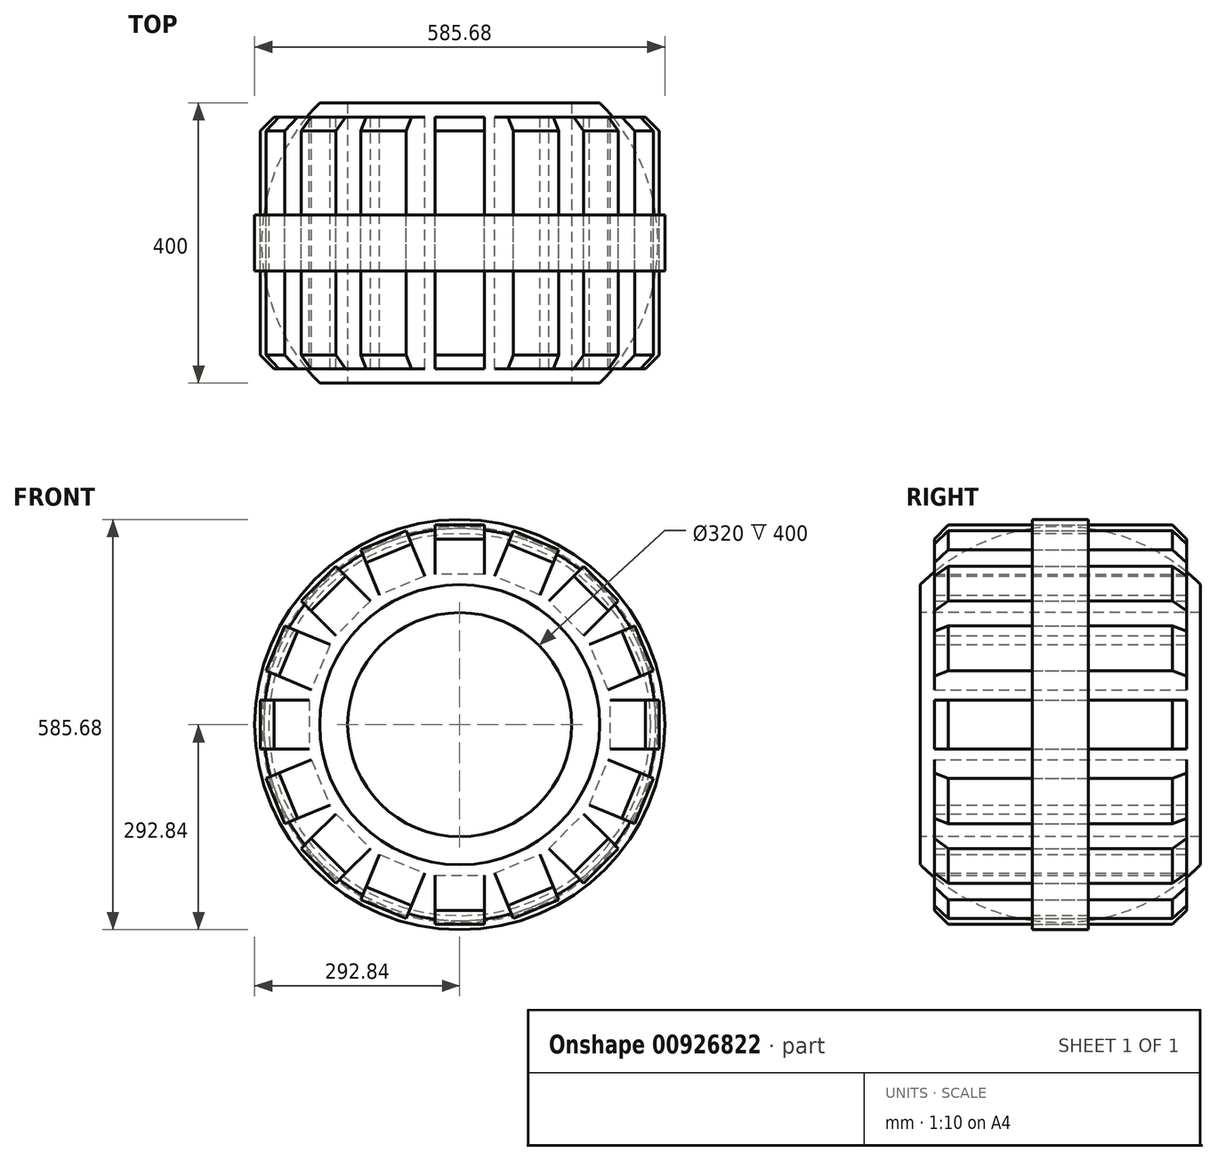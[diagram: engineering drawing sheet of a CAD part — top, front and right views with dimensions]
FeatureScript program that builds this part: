
annotation { "Feature Type Name" : "Feature", "Feature Type Description" : "" }
export const myFeature = defineFeature(function(context is Context, id is Id, definition is map)
    precondition{}
    {
        {
            var Q0;
            Q0=qCreatedBy(makeId("Top.planeOp"),FACE);
            var sketch = newSketch(context, id + "F0", { "sketchPlane" : qUnion([Q0])});
            skLineSegment(sketch, "E0", {"start": v(0, 0) * mm, "end": v(0, 200) * mm});
            skLineSegment(sketch, "E1", {"start": v(0, 200) * mm, "end": v(200, 200) * mm});
            skLineSegment(sketch, "E2", {"start": v(0, 0) * mm, "end": v(0, -200) * mm});
            skLineSegment(sketch, "E3", {"start": v(0, -200) * mm, "end": v(200, -200) * mm});
            skArc(sketch, "E4", {"start": v(200, -200) * mm, "mid": v(282.84, 0) * mm, "end": v(200, 200) * mm});
            skLineSegment(sketch, "E5", {"start": v(160, -200) * mm, "end": v(160, 200) * mm});
            skLineSegment(sketch, "E6", {"start": v(0, 0) * mm, "end": v(282.84, 0) * mm});
            skLineSegment(sketch, "E7.bottom", {"start": v(292.84, 40) * mm, "end": v(272.84, 40) * mm});
            skLineSegment(sketch, "E7.top", {"start": v(292.84, -40) * mm, "end": v(272.84, -40) * mm});
            skLineSegment(sketch, "E7.left", {"start": v(292.84, 40) * mm, "end": v(292.84, -40) * mm});
            skLineSegment(sketch, "E7.right", {"start": v(272.84, 40) * mm, "end": v(272.84, -40) * mm});
            skPoint(sketch, "E7.middle", {"position": v(282.84, 0) * mm});
            skSolve(sketch);
        }
        {
            var Q0;
            {var subQ5=sQuery(id+"F0.wireOp",EDGE,"E4");var subQ6=sQuery(id+"F0.wireOp",EDGE,"E1");var subQ7=makeQuery(id+"F0.imprint","INTERSECT",VERTEX,{"derivedFrom":[subQ6,subQ5]});Q0=makeQuery(id+"F0.imprint","IMPRINT",FACE,{"disambiguationData":[TD([[makeQuery(id+"F0.imprint","IMPRINT",EDGE,{"disambiguationData":[TD([[subQ7,1.0]])],"derivedFrom":subQ6}),-1.0]])]});}
            var Q1;
            {var subQ0=sQuery(id+"F0.wireOp",EDGE,"E7.left");Q1=makeQuery(id+"F0.imprint","IMPRINT",FACE,{"disambiguationData":[TD([[makeQuery(id+"F0.imprint","IMPRINT",EDGE,{"derivedFrom":subQ0}),-1.0]])]});}
            var Q2;
            {var subQ5=sQuery(id+"F0.wireOp",EDGE,"E4");var subQ6=sQuery(id+"F0.wireOp",EDGE,"E3");var subQ7=makeQuery(id+"F0.imprint","INTERSECT",VERTEX,{"derivedFrom":[subQ6,subQ5]});Q2=makeQuery(id+"F0.imprint","IMPRINT",FACE,{"disambiguationData":[TD([[makeQuery(id+"F0.imprint","IMPRINT",EDGE,{"disambiguationData":[TD([[subQ7,1.0]])],"derivedFrom":subQ6}),1.0]])]});}
            var Q3;
            Q3=sQuery(id+"F0.wireOp",EDGE,"E0");
            revolve(context, id + "F1", {"surfaceOperationType" : NewSurfaceOperationType.NEW, "entities" : qUnion([Q0, Q1, Q2]), "axis" : qUnion([Q3]), "revolveType" : RevolveType.FULL});
        }
        {
            var Q0;
            Q0=qCreatedBy(makeId("Front.planeOp"),FACE);
            var sketch = newSketch(context, id + "F2", { "sketchPlane" : qUnion([Q0])});
            skLineSegment(sketch, "E8", {"start": v(0, 0) * mm, "end": v(0, 250) * mm});
            skLineSegment(sketch, "E9.bottom", {"start": v(35, 285) * mm, "end": v(-35, 285) * mm});
            skLineSegment(sketch, "E9.top", {"start": v(35, 215) * mm, "end": v(-35, 215) * mm});
            skLineSegment(sketch, "E9.left", {"start": v(35, 285) * mm, "end": v(35, 215) * mm});
            skLineSegment(sketch, "E9.right", {"start": v(-35, 285) * mm, "end": v(-35, 215) * mm});
            skPoint(sketch, "E9.middle", {"position": v(0, 250) * mm});
            skSolve(sketch);
        }
        {
            var Q0;
            Q0 = qSketchRegion(id + "F2", true);
            extrude(context, id + "F3", {"entities" : qUnion([Q0]), "endBound" : BoundingType.SYMMETRIC, "depth" : 360 * mm, "offsetDistance" : 25 * mm});
        }
        {
            var Q0;
            Q0=makeQuery(id+"F3.opExtrude","CAP_EDGE",EDGE,{"disambiguationData":[OSD([sQuery(id+"F2.wireOp",EDGE,"E9.bottom")])],"isStart":false});
            chamfer(context, id + "F4", {"entities" : qUnion([Q0]), "width" : 20 * mm, "tangentPropagation" : true});
        }
        {
            var Q0;
            Q0=makeQuery(id+"F3.opExtrude","CAP_EDGE",EDGE,{"disambiguationData":[OSD([sQuery(id+"F2.wireOp",EDGE,"E9.bottom")])],"isStart":true});
            chamfer(context, id + "F5", {"entities" : qUnion([Q0]), "width" : 20 * mm, "tangentPropagation" : true});
        }
        {
            var Q0;
            Q0=makeQuery(id+"F3.opExtrude","SWEPT_BODY",BODY,{"disambiguationData":[OSD([sQuery(id+"F2.wireOp",EDGE,"E9.bottom"),sQuery(id+"F2.wireOp",EDGE,"E9.top"),sQuery(id+"F2.wireOp",EDGE,"E9.left"),sQuery(id+"F2.wireOp",EDGE,"E9.right")])]});
            var Q1;
            Q1=makeQuery(id+"F1.opRevolve","SWEPT_FACE",FACE,{"disambiguationData":[OSD([sQuery(id+"F0.wireOp",EDGE,"E7.left")])]});
            circularPattern(context, id + "F6", {"entities" : qUnion([Q0]), "axis" : qUnion([Q1]), "angle" : 360 * degree, "instanceCount" : 16, "equalSpace" : true});
        }
    });
